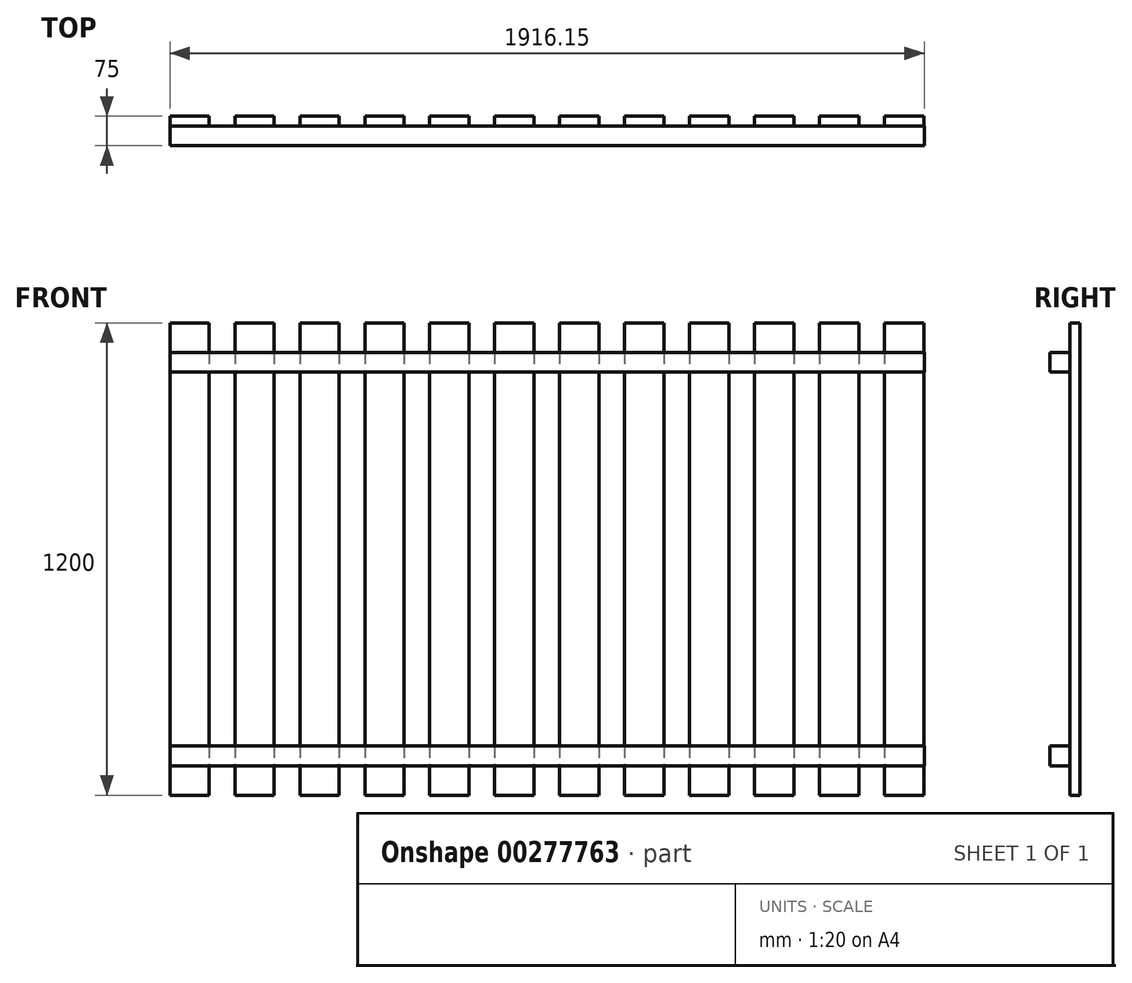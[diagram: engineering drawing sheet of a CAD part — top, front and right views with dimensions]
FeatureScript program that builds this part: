
annotation { "Feature Type Name" : "Feature", "Feature Type Description" : "" }
export const myFeature = defineFeature(function(context is Context, id is Id, definition is map)
    precondition{}
    {
        {
            var Q0;
            Q0=qCreatedBy(makeId("Front.planeOp"),FACE);
            var sketch = newSketch(context, id + "F0", { "sketchPlane" : qUnion([Q0])});
            skLineSegment(sketch, "E0.bottom", {"start": v(-101.95, 847.9) * mm, "end": v(-1.95, 847.9) * mm});
            skLineSegment(sketch, "E0.top", {"start": v(-101.95, -352.1) * mm, "end": v(-1.95, -352.1) * mm});
            skLineSegment(sketch, "E0.left", {"start": v(-101.95, 847.9) * mm, "end": v(-101.95, -352.1) * mm});
            skLineSegment(sketch, "E0.right", {"start": v(-1.95, 847.9) * mm, "end": v(-1.95, -352.1) * mm});
            skLineSegment(sketch, "E1.1.0.0", {"start": v(63.05, 847.9) * mm, "end": v(63.05, -352.1) * mm});
            skLineSegment(sketch, "E1.1.0.1", {"start": v(163.05, 847.9) * mm, "end": v(163.05, -352.1) * mm});
            skLineSegment(sketch, "E1.1.0.2", {"start": v(63.05, 847.9) * mm, "end": v(163.05, 847.9) * mm});
            skLineSegment(sketch, "E1.1.0.3", {"start": v(63.05, -352.1) * mm, "end": v(163.05, -352.1) * mm});
            skLineSegment(sketch, "E1.2.0.0", {"start": v(228.05, 847.9) * mm, "end": v(228.05, -352.1) * mm});
            skLineSegment(sketch, "E1.2.0.1", {"start": v(328.05, 847.9) * mm, "end": v(328.05, -352.1) * mm});
            skLineSegment(sketch, "E1.2.0.2", {"start": v(228.05, 847.9) * mm, "end": v(328.05, 847.9) * mm});
            skLineSegment(sketch, "E1.2.0.3", {"start": v(228.05, -352.1) * mm, "end": v(328.05, -352.1) * mm});
            skLineSegment(sketch, "E1.3.0.0", {"start": v(393.05, 847.9) * mm, "end": v(393.05, -352.1) * mm});
            skLineSegment(sketch, "E1.3.0.1", {"start": v(493.05, 847.9) * mm, "end": v(493.05, -352.1) * mm});
            skLineSegment(sketch, "E1.3.0.2", {"start": v(393.05, 847.9) * mm, "end": v(493.05, 847.9) * mm});
            skLineSegment(sketch, "E1.3.0.3", {"start": v(393.05, -352.1) * mm, "end": v(493.05, -352.1) * mm});
            skLineSegment(sketch, "E1.4.0.0", {"start": v(558.05, 847.9) * mm, "end": v(558.05, -352.1) * mm});
            skLineSegment(sketch, "E1.4.0.1", {"start": v(658.05, 847.9) * mm, "end": v(658.05, -352.1) * mm});
            skLineSegment(sketch, "E1.4.0.2", {"start": v(558.05, 847.9) * mm, "end": v(658.05, 847.9) * mm});
            skLineSegment(sketch, "E1.4.0.3", {"start": v(558.05, -352.1) * mm, "end": v(658.05, -352.1) * mm});
            skLineSegment(sketch, "E1.5.0.0", {"start": v(723.05, 847.9) * mm, "end": v(723.05, -352.1) * mm});
            skLineSegment(sketch, "E1.5.0.1", {"start": v(823.05, 847.9) * mm, "end": v(823.05, -352.1) * mm});
            skLineSegment(sketch, "E1.5.0.2", {"start": v(723.05, 847.9) * mm, "end": v(823.05, 847.9) * mm});
            skLineSegment(sketch, "E1.5.0.3", {"start": v(723.05, -352.1) * mm, "end": v(823.05, -352.1) * mm});
            skLineSegment(sketch, "E1.6.0.0", {"start": v(888.05, 847.9) * mm, "end": v(888.05, -352.1) * mm});
            skLineSegment(sketch, "E1.6.0.1", {"start": v(988.05, 847.9) * mm, "end": v(988.05, -352.1) * mm});
            skLineSegment(sketch, "E1.6.0.2", {"start": v(888.05, 847.9) * mm, "end": v(988.05, 847.9) * mm});
            skLineSegment(sketch, "E1.6.0.3", {"start": v(888.05, -352.1) * mm, "end": v(988.05, -352.1) * mm});
            skLineSegment(sketch, "E1.7.0.0", {"start": v(1053.05, 847.9) * mm, "end": v(1053.05, -352.1) * mm});
            skLineSegment(sketch, "E1.7.0.1", {"start": v(1153.05, 847.9) * mm, "end": v(1153.05, -352.1) * mm});
            skLineSegment(sketch, "E1.7.0.2", {"start": v(1053.05, 847.9) * mm, "end": v(1153.05, 847.9) * mm});
            skLineSegment(sketch, "E1.7.0.3", {"start": v(1053.05, -352.1) * mm, "end": v(1153.05, -352.1) * mm});
            skLineSegment(sketch, "E1.8.0.0", {"start": v(1218.05, 847.9) * mm, "end": v(1218.05, -352.1) * mm});
            skLineSegment(sketch, "E1.8.0.1", {"start": v(1318.05, 847.9) * mm, "end": v(1318.05, -352.1) * mm});
            skLineSegment(sketch, "E1.8.0.2", {"start": v(1218.05, 847.9) * mm, "end": v(1318.05, 847.9) * mm});
            skLineSegment(sketch, "E1.8.0.3", {"start": v(1218.05, -352.1) * mm, "end": v(1318.05, -352.1) * mm});
            skLineSegment(sketch, "E1.9.0.0", {"start": v(1383.05, 847.9) * mm, "end": v(1383.05, -352.1) * mm});
            skLineSegment(sketch, "E1.9.0.1", {"start": v(1483.05, 847.9) * mm, "end": v(1483.05, -352.1) * mm});
            skLineSegment(sketch, "E1.9.0.2", {"start": v(1383.05, 847.9) * mm, "end": v(1483.05, 847.9) * mm});
            skLineSegment(sketch, "E1.9.0.3", {"start": v(1383.05, -352.1) * mm, "end": v(1483.05, -352.1) * mm});
            skLineSegment(sketch, "E1.10.0.0", {"start": v(1548.05, 847.9) * mm, "end": v(1548.05, -352.1) * mm});
            skLineSegment(sketch, "E1.10.0.1", {"start": v(1648.05, 847.9) * mm, "end": v(1648.05, -352.1) * mm});
            skLineSegment(sketch, "E1.10.0.2", {"start": v(1548.05, 847.9) * mm, "end": v(1648.05, 847.9) * mm});
            skLineSegment(sketch, "E1.10.0.3", {"start": v(1548.05, -352.1) * mm, "end": v(1648.05, -352.1) * mm});
            skLineSegment(sketch, "E1.11.0.0", {"start": v(1713.05, 847.9) * mm, "end": v(1713.05, -352.1) * mm});
            skLineSegment(sketch, "E1.11.0.1", {"start": v(1813.05, 847.9) * mm, "end": v(1813.05, -352.1) * mm});
            skLineSegment(sketch, "E1.11.0.2", {"start": v(1713.05, 847.9) * mm, "end": v(1813.05, 847.9) * mm});
            skLineSegment(sketch, "E1.11.0.3", {"start": v(1713.05, -352.1) * mm, "end": v(1813.05, -352.1) * mm});
            skLineSegment(sketch, "E1.direction1", {"start": v(-101.95, -352.1) * mm, "end": v(63.05, -352.1) * mm, "construction": true});
            skSolve(sketch);
        }
        {
            var Q0;
            Q0=makeQuery(id+"F0.imprint","IMPRINT",FACE,{"disambiguationData":[TD([[makeQuery(id+"F0.imprint","IMPRINT",EDGE,{"derivedFrom":sQuery(id+"F0.wireOp",EDGE,"E1.1.0.0")}),1.0]])]});
            var Q1;
            Q1=makeQuery(id+"F0.imprint","IMPRINT",FACE,{"disambiguationData":[TD([[makeQuery(id+"F0.imprint","IMPRINT",EDGE,{"derivedFrom":sQuery(id+"F0.wireOp",EDGE,"E1.2.0.0")}),1.0]])]});
            var Q2;
            Q2=makeQuery(id+"F0.imprint","IMPRINT",FACE,{"disambiguationData":[TD([[makeQuery(id+"F0.imprint","IMPRINT",EDGE,{"derivedFrom":sQuery(id+"F0.wireOp",EDGE,"E1.3.0.0")}),1.0]])]});
            var Q3;
            Q3=makeQuery(id+"F0.imprint","IMPRINT",FACE,{"disambiguationData":[TD([[makeQuery(id+"F0.imprint","IMPRINT",EDGE,{"derivedFrom":sQuery(id+"F0.wireOp",EDGE,"E1.4.0.0")}),1.0]])]});
            var Q4;
            Q4=makeQuery(id+"F0.imprint","IMPRINT",FACE,{"disambiguationData":[TD([[makeQuery(id+"F0.imprint","IMPRINT",EDGE,{"derivedFrom":sQuery(id+"F0.wireOp",EDGE,"E1.5.0.0")}),1.0]])]});
            var Q5;
            Q5=makeQuery(id+"F0.imprint","IMPRINT",FACE,{"disambiguationData":[TD([[makeQuery(id+"F0.imprint","IMPRINT",EDGE,{"derivedFrom":sQuery(id+"F0.wireOp",EDGE,"E1.6.0.0")}),1.0]])]});
            var Q6;
            Q6=makeQuery(id+"F0.imprint","IMPRINT",FACE,{"disambiguationData":[TD([[makeQuery(id+"F0.imprint","IMPRINT",EDGE,{"derivedFrom":sQuery(id+"F0.wireOp",EDGE,"E1.7.0.0")}),1.0]])]});
            var Q7;
            Q7=makeQuery(id+"F0.imprint","IMPRINT",FACE,{"disambiguationData":[TD([[makeQuery(id+"F0.imprint","IMPRINT",EDGE,{"derivedFrom":sQuery(id+"F0.wireOp",EDGE,"E1.8.0.0")}),1.0]])]});
            var Q8;
            Q8=makeQuery(id+"F0.imprint","IMPRINT",FACE,{"disambiguationData":[TD([[makeQuery(id+"F0.imprint","IMPRINT",EDGE,{"derivedFrom":sQuery(id+"F0.wireOp",EDGE,"E1.9.0.0")}),1.0]])]});
            var Q9;
            Q9=makeQuery(id+"F0.imprint","IMPRINT",FACE,{"disambiguationData":[TD([[makeQuery(id+"F0.imprint","IMPRINT",EDGE,{"derivedFrom":sQuery(id+"F0.wireOp",EDGE,"E1.10.0.0")}),1.0]])]});
            var Q10;
            Q10=makeQuery(id+"F0.imprint","IMPRINT",FACE,{"disambiguationData":[TD([[makeQuery(id+"F0.imprint","IMPRINT",EDGE,{"derivedFrom":sQuery(id+"F0.wireOp",EDGE,"E1.11.0.0")}),1.0]])]});
            var Q11;
            Q11=makeQuery(id+"F0.imprint","IMPRINT",FACE,{"disambiguationData":[TD([[makeQuery(id+"F0.imprint","IMPRINT",EDGE,{"derivedFrom":sQuery(id+"F0.wireOp",EDGE,"E0.bottom")}),-1.0]])]});
            extrude(context, id + "F1", {"entities" : qUnion([Q0, Q1, Q2, Q3, Q4, Q5, Q6, Q7, Q8, Q9, Q10, Q11]), "depth" : 25 * mm});
        }
        {
            var Q0;
            Q0=makeQuery(id+"F1.opExtrude","CAP_FACE",FACE,{"disambiguationData":[OSD([sQuery(id+"F0.wireOp",EDGE,"E0.bottom"),sQuery(id+"F0.wireOp",EDGE,"E0.top"),sQuery(id+"F0.wireOp",EDGE,"E0.left"),sQuery(id+"F0.wireOp",EDGE,"E0.right")])],"isStart":false});
            var sketch = newSketch(context, id + "F2", { "sketchPlane" : qUnion([Q0])});
            skLineSegment(sketch, "E2.bottom", {"start": v(-101.95, 722.9) * mm, "end": v(1814.2, 722.9) * mm});
            skLineSegment(sketch, "E2.top", {"start": v(-101.95, 772.9) * mm, "end": v(1814.2, 772.9) * mm});
            skLineSegment(sketch, "E2.left", {"start": v(-101.95, 722.9) * mm, "end": v(-101.95, 772.9) * mm});
            skLineSegment(sketch, "E2.right", {"start": v(1814.2, 722.9) * mm, "end": v(1814.2, 772.9) * mm});
            skLineSegment(sketch, "E3.0.1.0", {"start": v(-101.95, -227.1) * mm, "end": v(1814.2, -227.1) * mm});
            skLineSegment(sketch, "E3.0.1.1", {"start": v(-101.95, -277.1) * mm, "end": v(-101.95, -227.1) * mm});
            skLineSegment(sketch, "E3.0.1.2", {"start": v(-101.95, -277.1) * mm, "end": v(1814.2, -277.1) * mm});
            skLineSegment(sketch, "E3.0.1.3", {"start": v(1814.2, -277.1) * mm, "end": v(1814.2, -227.1) * mm});
            skLineSegment(sketch, "E3.direction2", {"start": v(-101.95, 772.9) * mm, "end": v(-101.95, -227.1) * mm, "construction": true});
            skSolve(sketch);
        }
        {
            var Q0;
            Q0 = qSketchRegion(id + "F2", true);
            extrude(context, id + "F3", {"entities" : qUnion([Q0]), "depth" : 50 * mm});
        }
    });
